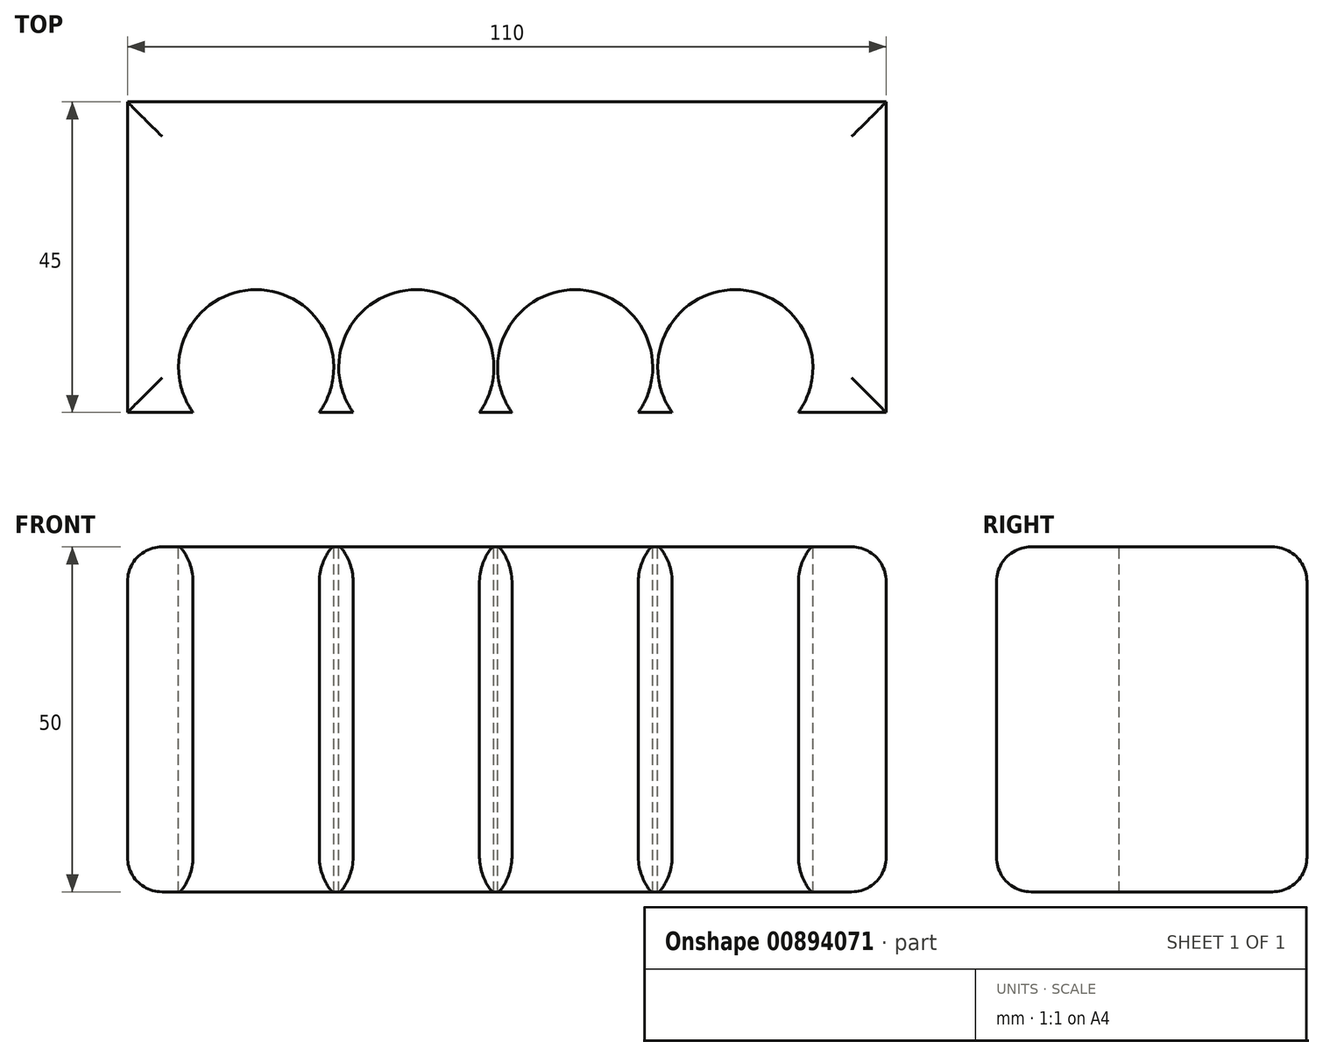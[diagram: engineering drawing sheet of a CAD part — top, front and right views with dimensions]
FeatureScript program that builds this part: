
annotation { "Feature Type Name" : "Feature", "Feature Type Description" : "" }
export const myFeature = defineFeature(function(context is Context, id is Id, definition is map)
    precondition{}
    {
        {
            var Q0;
            Q0=qCreatedBy(makeId("Front.planeOp"),FACE);
            var sketch = newSketch(context, id + "F0", { "sketchPlane" : qUnion([Q0])});
            skLineSegment(sketch, "E0.bottom", {"start": v(-33.08, 22.35) * mm, "end": v(76.92, 22.35) * mm});
            skLineSegment(sketch, "E0.top", {"start": v(-33.08, -27.65) * mm, "end": v(76.92, -27.65) * mm});
            skLineSegment(sketch, "E0.left", {"start": v(-33.08, 22.35) * mm, "end": v(-33.08, -27.65) * mm});
            skLineSegment(sketch, "E0.right", {"start": v(76.92, 22.35) * mm, "end": v(76.92, -27.65) * mm});
            skSolve(sketch);
        }
        {
            var Q0;
            Q0 = qSketchRegion(id + "F0", true);
            extrude(context, id + "F1", {"entities" : qUnion([Q0]), "depth" : 45 * mm, "offsetDistance" : 25 * mm});
        }
        {
            var Q0;
            Q0=makeQuery(id+"F1.opExtrude","SWEPT_FACE",FACE,{"disambiguationData":[OSD([sQuery(id+"F0.wireOp",EDGE,"E0.bottom")])]});
            var Q1;
            Q1=makeQuery(id+"F1.opExtrude","SWEPT_FACE",FACE,{"disambiguationData":[OSD([sQuery(id+"F0.wireOp",EDGE,"E0.top")])]});
            fillet(context, id + "F2", {"entities" : qUnion([Q0, Q1]), "radius" : 5 * mm, "tangentPropagation" : true, "allowEdgeOverflow" : false});
        }
        {
            var Q0;
            Q0=qCreatedBy(makeId("Top.planeOp"),FACE);
            var sketch = newSketch(context, id + "F3", { "sketchPlane" : qUnion([Q0])});
            skCircle(sketch, "E1", {"center": v(-14.42, -38.47) * mm, "radius": 11.25 * mm});
            skCircle(sketch, "E2", {"center": v(8.8, -38.47) * mm, "radius": 11.25 * mm});
            skCircle(sketch, "E3", {"center": v(31.82, -38.47) * mm, "radius": 11.25 * mm});
            skCircle(sketch, "E4", {"center": v(55.04, -38.47) * mm, "radius": 11.25 * mm});
            skSolve(sketch);
        }
        {
            var Q0;
            Q0 = qSketchRegion(id + "F3", true);
            extrude(context, id + "F4", {"entities" : qUnion([Q0]), "operationType" : NewBodyOperationType.REMOVE, "oppositeDirection" : true, "depth" : 50 * mm, "offsetDistance" : 25 * mm});
        }
        {
            var Q0;
            Q0 = qSketchRegion(id + "F3", true);
            extrude(context, id + "F5", {"entities" : qUnion([Q0]), "operationType" : NewBodyOperationType.REMOVE, "depth" : 25 * mm, "offsetDistance" : 25 * mm});
        }
    });
